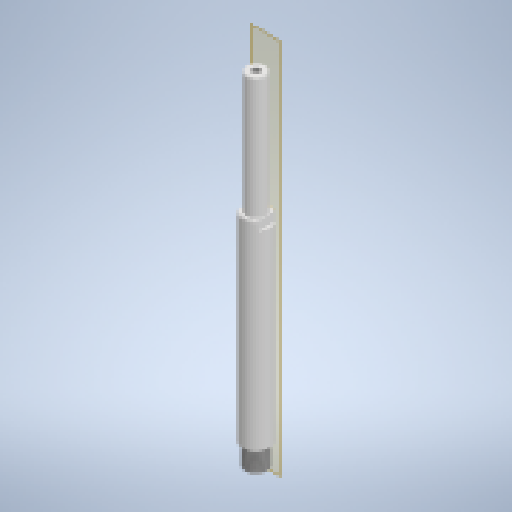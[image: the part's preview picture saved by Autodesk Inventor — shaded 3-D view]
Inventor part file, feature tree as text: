
AUTODESK INVENTOR PART (.ipt)
format: ipt  version: 2023.2 (Build 272271030, 271C)  size: 208,896 bytes
history: native  units: mm
features: sketch x4, other x2, extrude x2, projected_geometry x2, revolve x1, hole x1, thread x1, chamfer x1
ambient origin geometry x8: Origin, YZ Plane, XZ Plane, XY Plane, X Axis, Y Axis, Z Axis, Center Point
bodies: Body1 (feature_tree)
feature tree (14):
  other  "Твердое тело1"
  revolve  "Вращение1"
  hole  "Отверстие1"  [1 undecoded]
  thread  "Резьба1"
  other  "РабПлоскость1"
  extrude  "Выдавливание1"  Depth=19.0mm
  chamfer  "Chamfer1"  Angle=360.0deg  [1 undecoded]
  extrude  "Extrusion2"  Depth=19.0mm
  sketch  "Эскиз1"
  sketch  "Эскиз2"
  sketch  "Эскиз3"
  sketch  "Sketch4"  dims[d1=200.0mm d2=18.0mm d3=25.0mm d5=360.0deg d7=25.0mm d8=137.0mm d9=6.647mm d10=25.0mm d11=4.0mm d12=2.0mm d13=90.0deg d14=30.0mm d15=20.594885mm d16=180.0mm d17=20.0mm d18=20.0mm d19=20.0mm d20=0.0mm d21=10.0mm d22=70.0mm d23=5.1mm d24=2.0mm d25=0.0mm d26=1.0mm d27=2.0mm d28=45.0deg d29=19.0mm d30=8.0mm d31=0.0mm d32=0.0mm]
  projected_geometry  "Projected Loop1"
  projected_geometry  "Projected Loop2"
note: 2 required parameter values undecoded (feature->parameter linkage not recoverable at this tier; creation-order binding heuristic only, values carry confidence <= 0.55)
